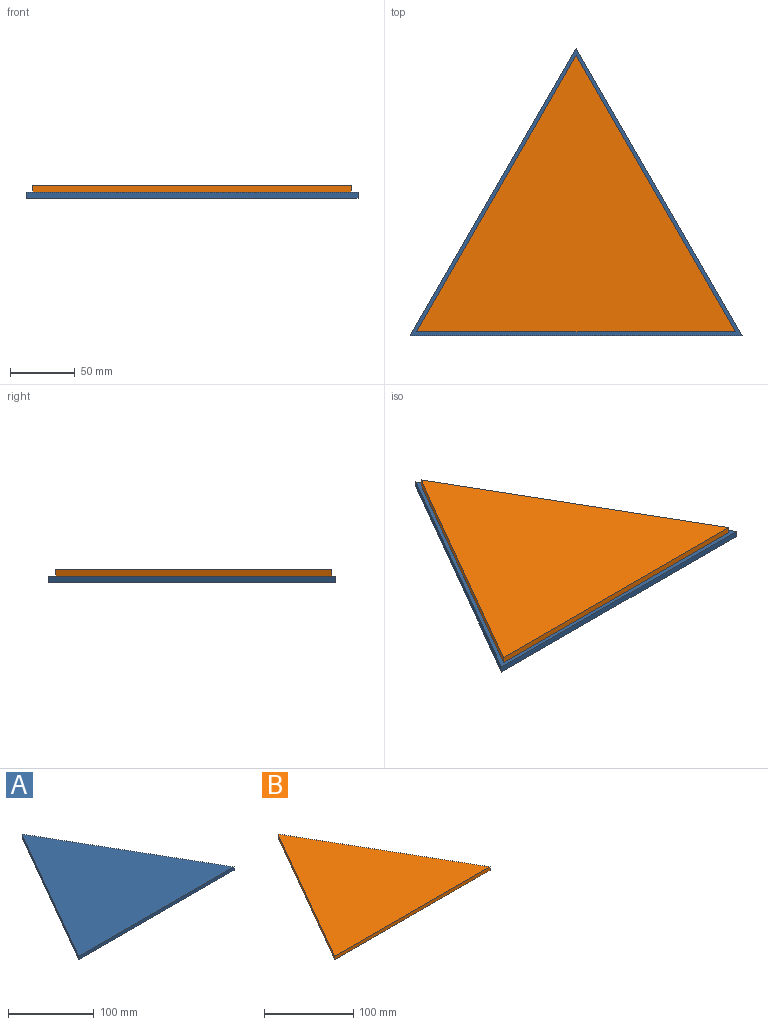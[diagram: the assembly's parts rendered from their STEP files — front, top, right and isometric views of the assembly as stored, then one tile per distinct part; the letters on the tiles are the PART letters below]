
ASSEMBLY  parts=2 mates=1
PART A: 5 faces, bbox 256.6x222.3x4.8 mm
  f0: plane 256.63x4.76mm, normal (0,-1,0), area 1222.2mm2, adj f1,f2,f3,f4
  f1: plane 222.25x128.32mm, normal (0.87,0.5,0), area 1222.2mm2, adj f0,f2,f3,f4
  f2: plane 222.25x128.32mm, normal (-0.87,0.5,0), area 1222.2mm2, adj f0,f1,f3,f4
  f3: plane 256.63x222.25mm, normal (0,0,1), area 28518.3mm2, adj f0,f1,f2
  f4: plane 256.63x222.25mm, normal (0,0,-1), area 28518.3mm2, adj f0,f1,f2
PART B: 5 faces, bbox 246.4x213.4x4.8 mm
  f0: plane 246.37x4.76mm, normal (0,-1,0), area 1173.3mm2, adj f1,f2,f3,f4
  f1: plane 213.36x123.18mm, normal (0.87,0.5,0), area 1173.3mm2, adj f0,f2,f3,f4
  f2: plane 213.36x123.18mm, normal (-0.87,0.5,0), area 1173.3mm2, adj f0,f1,f3,f4
  f3: plane 246.37x213.36mm, normal (0,0,1), area 26282.4mm2, adj f0,f1,f2
  f4: plane 246.37x213.36mm, normal (0,0,-1), area 26282.4mm2, adj f0,f1,f2
PLACE A t=(-3529.28,-111.12,-7.14)mm
PLACE B t=(-3288.05,-112.61,-2.38)mm
MATE parallel B.f4 <-> A.f3  axis (0,0,-1) through (0,-148.17,0)mm
